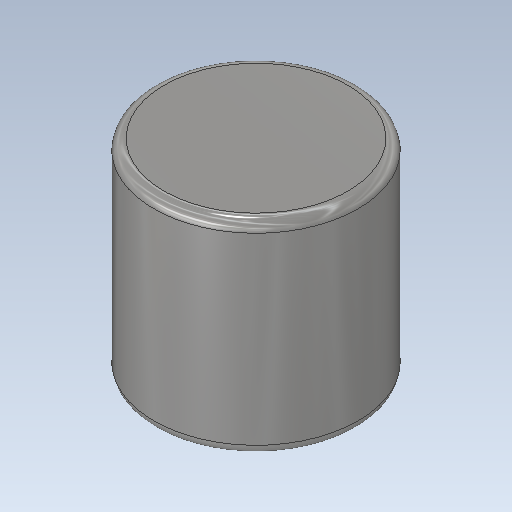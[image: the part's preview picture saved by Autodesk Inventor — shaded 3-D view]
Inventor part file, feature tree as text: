
AUTODESK INVENTOR PART (.ipt)
format: ipt  version: 2020.1 (Build 241239000, 239)  size: 135,168 bytes
history: native  units: mm
features: extrude x1, fillet x1, sketch x1
ambient origin geometry x8: Origin, YZ Plane, XZ Plane, XY Plane, X Axis, Y Axis, Z Axis, Center Point
bodies: Solid1 (feature_tree)
feature tree (3):
  extrude  "Extrusion1"  Depth=5.0mm TaperAngle=0.0deg
  fillet  "Fillet1"  Radius=0.25mm
  sketch  "Sketch1"  dims[d0=5.0mm d1=5.0mm d2=0.0mm d3=0.25mm]
